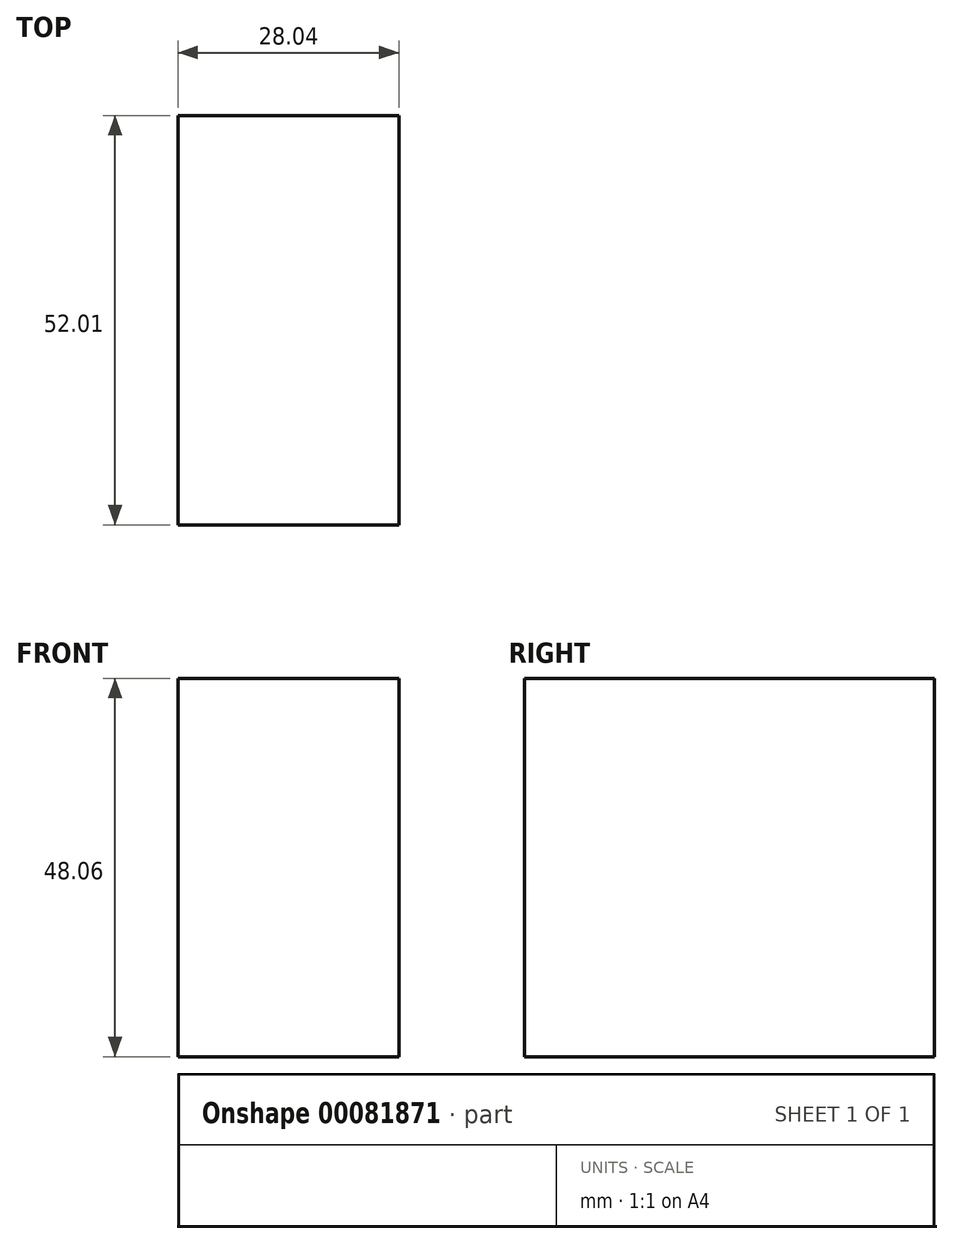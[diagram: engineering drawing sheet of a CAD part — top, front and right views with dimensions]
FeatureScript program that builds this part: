
annotation { "Feature Type Name" : "Feature", "Feature Type Description" : "" }
export const myFeature = defineFeature(function(context is Context, id is Id, definition is map)
    precondition{}
    {
        {
            var Q0;
            Q0=qCreatedBy(makeId("Top.planeOp"),FACE);
            var sketch = newSketch(context, id + "F0", { "sketchPlane" : qUnion([Q0])});
            skLineSegment(sketch, "E0.bottom", {"start": v(0, 52.01) * mm, "end": v(28.04, 52.01) * mm});
            skLineSegment(sketch, "E0.top", {"start": v(0, 0) * mm, "end": v(28.04, 0) * mm});
            skLineSegment(sketch, "E0.left", {"start": v(0, 52.01) * mm, "end": v(0, 0) * mm});
            skLineSegment(sketch, "E0.right", {"start": v(28.04, 52.01) * mm, "end": v(28.04, 0) * mm});
            skSolve(sketch);
        }
        {
            var Q0;
            Q0=makeQuery(id+"F0.imprint","IMPRINT",FACE,{"disambiguationData":[TD([[makeQuery(id+"F0.imprint","IMPRINT",EDGE,{"derivedFrom":sQuery(id+"F0.wireOp",EDGE,"E0.bottom")}),-1.0]])]});
            extrude(context, id + "F1", {"entities" : qUnion([Q0]), "depth" : 48.06 * mm});
        }
    });
